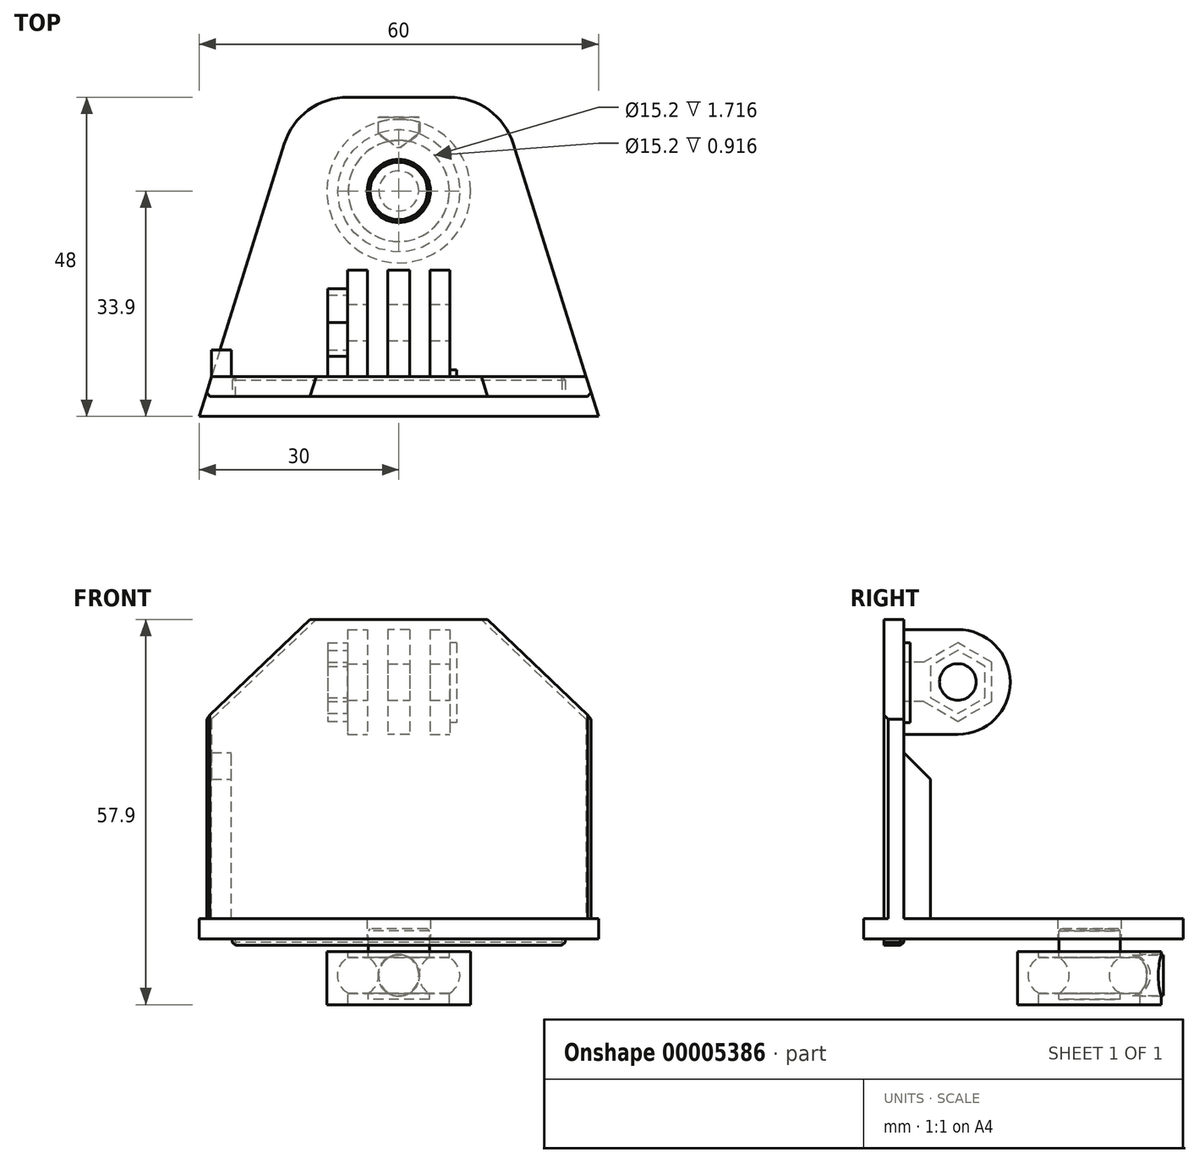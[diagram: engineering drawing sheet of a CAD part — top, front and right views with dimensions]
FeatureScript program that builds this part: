
annotation { "Feature Type Name" : "Feature", "Feature Type Description" : "" }
export const myFeature = defineFeature(function(context is Context, id is Id, definition is map)
    precondition{}
    {
        {
            var Q0;
            Q0=qCreatedBy(makeId("Top.planeOp"),FACE);
            var sketch = newSketch(context, id + "F0", { "sketchPlane" : qUnion([Q0])});
            skArc(sketch, "E0", {"start": v(3, 0) * mm, "mid": v(0, 3) * mm, "end": v(-3, 0) * mm});
            skLineSegment(sketch, "E1", {"start": v(3, 0) * mm, "end": v(-3, 0) * mm});
            skLineSegment(sketch, "E2", {"start": v(0, 0) * mm, "end": v(0, -6.1) * mm, "construction": true});
            skSolve(sketch);
        }
        {
            var Q0;
            Q0=qCreatedBy(makeId("Right.planeOp"),FACE);
            var sketch = newSketch(context, id + "F1", { "sketchPlane" : qUnion([Q0])});
            skCircle(sketch, "E3", {"center": v(0, 0) * mm, "radius": 3.08 * mm});
            skLineSegment(sketch, "E4", {"start": v(0, 0) * mm, "end": v(-12.4, 0) * mm, "construction": true});
            skLineSegment(sketch, "E5", {"start": v(-12.4, 8.14) * mm, "end": v(-12.4, -5.03) * mm, "construction": true});
            skLineSegment(sketch, "E6", {"start": v(0, 0) * mm, "end": v(0, 3.76) * mm, "construction": true});
            skLineSegment(sketch, "E7", {"start": v(-6.1, 3.76) * mm, "end": v(-6.1, -2.41) * mm, "construction": true});
            skSolve(sketch);
        }
        {
            var Q0;
            Q0=sQuery(id+"F1.wireOp",EDGE,"E3");
            var Q1;
            Q1=sQuery(id+"F1.wireOp",EDGE,"E7");
            revolve(context, id + "F2", {"bodyType" : ToolBodyType.SURFACE, "surfaceEntities" : qUnion([Q0]), "axis" : qUnion([Q1]), "revolveType" : RevolveType.FULL});
        }
        {
            var Q0;
            Q0=qCreatedBy(makeId("Right.planeOp"),FACE);
            var sketch = newSketch(context, id + "F3", { "sketchPlane" : qUnion([Q0])});
            skCircle(sketch, "E8.0", {"center": v(0, 0) * mm, "radius": 3.08 * mm});
            skLineSegment(sketch, "E9.0", {"start": v(-6.1, 3.76) * mm, "end": v(-6.1, -2.41) * mm});
            skLineSegment(sketch, "E9.1", {"start": v(0, 0) * mm, "end": v(-12.4, 0) * mm});
            skPoint(sketch, "E10.rect.middle", {"position": v(-6.1, 0) * mm});
            skLineSegment(sketch, "E11", {"start": v(-1.5, 7) * mm, "end": v(-1.5, -3.6) * mm});
            skLineSegment(sketch, "E12", {"start": v(-1.5, -3.6) * mm, "end": v(-6.1, -3.6) * mm});
            skLineSegment(sketch, "E13", {"start": v(-6.1, -3.6) * mm, "end": v(-6.1, 7) * mm});
            skLineSegment(sketch, "E14", {"start": v(-6.1, 7) * mm, "end": v(-1.5, 7) * mm});
            skLineSegment(sketch, "E15", {"start": v(4.7, 3.6) * mm, "end": v(4.7, -4.4) * mm});
            skLineSegment(sketch, "E16", {"start": v(4.7, -4.4) * mm, "end": v(1.5, -4.4) * mm});
            skLineSegment(sketch, "E17", {"start": v(4.7, 3.6) * mm, "end": v(1.5, 3.6) * mm});
            skLineSegment(sketch, "E18", {"start": v(1.5, 3.6) * mm, "end": v(1.5, -4.4) * mm});
            skSolve(sketch);
        }
        {
            var Q0;
            {var subQ0=sQuery(id+"F3.wireOp",EDGE,"E14");Q0=makeQuery(id+"F3.imprint","IMPRINT",FACE,{"disambiguationData":[TD([[makeQuery(id+"F3.imprint","IMPRINT",EDGE,{"derivedFrom":subQ0}),-1.0]])]});}
            var Q1;
            {var subQ3=sQuery(id+"F3.wireOp",EDGE,"E12");Q1=makeQuery(id+"F3.imprint","IMPRINT",FACE,{"disambiguationData":[TD([[makeQuery(id+"F3.imprint","IMPRINT",EDGE,{"derivedFrom":subQ3}),-1.0]])]});}
            var Q2;
            Q2=sQuery(id+"F3.wireOp",EDGE,"E9.0");
            revolve(context, id + "F4", {"entities" : qUnion([Q0, Q1]), "axis" : qUnion([Q2]), "revolveType" : RevolveType.FULL});
        }
        {
            var Q0;
            Q0=makeQuery(id+"F3.imprint","IMPRINT",FACE,{"disambiguationData":[TD([[makeQuery(id+"F3.imprint","IMPRINT",EDGE,{"derivedFrom":sQuery(id+"F3.wireOp",EDGE,"E15")}),-1.0]])]});
            var Q1;
            Q1=sQuery(id+"F3.wireOp",EDGE,"E9.0");
            revolve(context, id + "F5", {"entities" : qUnion([Q0]), "axis" : qUnion([Q1]), "revolveType" : RevolveType.FULL});
        }
        {
            var Q0;
            Q0=qCreatedBy(makeId("Front.planeOp"),FACE);
            var sketch = newSketch(context, id + "F6", { "sketchPlane" : qUnion([Q0])});
            skCircle(sketch, "E19", {"center": v(0, 0) * mm, "radius": 3.15 * mm});
            skSolve(sketch);
        }
        {
            var Q0;
            Q0=makeQuery(id+"F6.imprint","IMPRINT",FACE,{"disambiguationData":[TD([[makeQuery(id+"F6.imprint","IMPRINT",EDGE,{"derivedFrom":sQuery(id+"F6.wireOp",EDGE,"E19")}),1.0]])]});
            var Q1;
            Q1=makeQuery(id+"F5.opRevolve","SWEPT_FACE",FACE,{"disambiguationData":[OSD([sQuery(id+"F3.wireOp",EDGE,"E15")])]});
            extrude(context, id + "F7", {"entities" : qUnion([Q0]), "operationType" : NewBodyOperationType.REMOVE, "endBound" : BoundingType.UP_TO_SURFACE, "oppositeDirection" : true, "endBoundEntityFace" : qUnion([Q1]), "depth" : 25 * mm});
        }
        {
            var Q0;
            Q0=qCreatedBy(makeId("Front.planeOp"),FACE);
            var sketch = newSketch(context, id + "F8", { "sketchPlane" : qUnion([Q0])});
            skLineSegment(sketch, "E20.rect.bottom", {"start": v(13.05, 1.97) * mm, "end": v(8.99, 1.97) * mm});
            skLineSegment(sketch, "E20.rect.top", {"start": v(13.05, 8.89) * mm, "end": v(8.99, 8.89) * mm});
            skLineSegment(sketch, "E20.rect.left", {"start": v(13.05, 1.97) * mm, "end": v(13.05, 8.89) * mm});
            skLineSegment(sketch, "E20.rect.right", {"start": v(8.99, 1.97) * mm, "end": v(8.99, 8.89) * mm});
            skPoint(sketch, "E20.rect.middle", {"position": v(11.02, 5.43) * mm});
            skSolve(sketch);
        }
        {
            var Q0;
            Q0=makeQuery(id+"F8.imprint","IMPRINT",FACE,{"disambiguationData":[TD([[makeQuery(id+"F8.imprint","IMPRINT",EDGE,{"derivedFrom":sQuery(id+"F8.wireOp",EDGE,"E20.rect.bottom")}),-1.0]])]});
            cPlane(context, id + "F9", {"entities" : qUnion([Q0]), "cplaneType" : CPlaneType.OFFSET, "offset" : 5 * mm, "oppositeDirection" : true, "width" : 150 * mm, "height" : 150 * mm});
        }
        {
            var Q0;
            Q0=qCreatedBy(id+"F9.planeOp",FACE);
            var sketch = newSketch(context, id + "F10", { "sketchPlane" : qUnion([Q0])});
            skCircle(sketch, "E21", {"center": v(0, 0) * mm, "radius": 3.05 * mm});
            skSolve(sketch);
        }
        {
            var Q0;
            Q0=makeQuery(id+"F10.imprint","IMPRINT",FACE,{"disambiguationData":[TD([[makeQuery(id+"F10.imprint","IMPRINT",EDGE,{"derivedFrom":sQuery(id+"F10.wireOp",EDGE,"E21")}),1.0]])]});
            var Q1;
            Q1=makeQuery(id+"F5.opRevolve","SWEPT_FACE",FACE,{"disambiguationData":[OSD([sQuery(id+"F3.wireOp",EDGE,"E8.0")])]});
            extrude(context, id + "F11", {"entities" : qUnion([Q0]), "endBound" : BoundingType.UP_TO_SURFACE, "endBoundEntityFace" : qUnion([Q1]), "depth" : 25 * mm});
        }
        {
            var Q0;
            Q0=makeQuery(id+"F4.opRevolve","SWEPT_EDGE",EDGE,{"disambiguationData":[OSD([sQuery(id+"F3.wireOp",EDGE,"E11"),sQuery(id+"F3.wireOp",EDGE,"E14")])]});
            chamfer(context, id + "F12", {"entities" : qUnion([Q0]), "width" : 0.3 * mm, "tangentPropagation" : true});
        }
        {
            var Q0;
            Q0=makeQuery(id+"F4.opRevolve","SWEPT_FACE",FACE,{"disambiguationData":[OSD([sQuery(id+"F3.wireOp",EDGE,"E14")])]});
            var sketch = newSketch(context, id + "F13", { "sketchPlane" : qUnion([Q0])});
            skLineSegment(sketch, "E22.bottom", {"start": v(-25, -34) * mm, "end": v(25, -34) * mm});
            skLineSegment(sketch, "E22.top", {"start": v(-25, -37) * mm, "end": v(25, -37) * mm});
            skLineSegment(sketch, "E22.left", {"start": v(-25, -34) * mm, "end": v(-25, -37) * mm});
            skLineSegment(sketch, "E22.right", {"start": v(25, -34) * mm, "end": v(25, -37) * mm});
            skLineSegment(sketch, "E23", {"start": v(-30, -40) * mm, "end": v(30, -40) * mm});
            skLineSegment(sketch, "E24", {"start": v(-15, 8) * mm, "end": v(15, 8) * mm});
            skLineSegment(sketch, "E25", {"start": v(-15, 8) * mm, "end": v(-30, -40) * mm});
            skLineSegment(sketch, "E26", {"start": v(15, 8) * mm, "end": v(30, -40) * mm});
            skCircle(sketch, "E27.0", {"center": v(0, -6.1) * mm, "radius": 4.75 * mm});
            skSolve(sketch);
        }
        {
            var Q0;
            Q0=makeQuery(id+"F13.imprint","IMPRINT",FACE,{"disambiguationData":[TD([[makeQuery(id+"F13.imprint","IMPRINT",EDGE,{"derivedFrom":sQuery(id+"F13.wireOp",EDGE,"E22.bottom")}),1.0]])]});
            extrude(context, id + "F14", {"entities" : qUnion([Q0]), "endBound" : BoundingType.SYMMETRIC, "depth" : 3 * mm});
        }
        {
            var Q0;
            Q0=makeQuery(id+"F14.opExtrude","SWEPT_EDGE",EDGE,{"disambiguationData":[OSD([sQuery(id+"F13.wireOp",EDGE,"E24"),sQuery(id+"F13.wireOp",EDGE,"E25")])]});
            var Q1;
            Q1=makeQuery(id+"F14.opExtrude","SWEPT_EDGE",EDGE,{"disambiguationData":[OSD([sQuery(id+"F13.wireOp",EDGE,"E24"),sQuery(id+"F13.wireOp",EDGE,"E26")])]});
            fillet(context, id + "F15", {"entities" : qUnion([Q0, Q1]), "radius" : 10 * mm, "tangentPropagation" : true, "allowEdgeOverflow" : false});
        }
        {
            var Q0;
            Q0=makeQuery(id+"F14.opExtrude","CAP_FACE",FACE,{"disambiguationData":[OSD([sQuery(id+"F13.wireOp",EDGE,"E22.bottom"),sQuery(id+"F13.wireOp",EDGE,"E22.top"),sQuery(id+"F13.wireOp",EDGE,"E22.left"),sQuery(id+"F13.wireOp",EDGE,"E22.right"),sQuery(id+"F13.wireOp",EDGE,"E23"),sQuery(id+"F13.wireOp",EDGE,"E24"),sQuery(id+"F13.wireOp",EDGE,"E25"),sQuery(id+"F13.wireOp",EDGE,"E26"),sQuery(id+"F13.wireOp",EDGE,"E27.0")])],"isStart":false});
            var sketch = newSketch(context, id + "F16", { "sketchPlane" : qUnion([Q0])});
            skLineSegment(sketch, "E28.0", {"start": v(-25, -37) * mm, "end": v(25, -37) * mm});
            skLineSegment(sketch, "E28.1", {"start": v(-25, -34) * mm, "end": v(-25, -37) * mm});
            skLineSegment(sketch, "E28.2", {"start": v(-25, -34) * mm, "end": v(25, -34) * mm});
            skLineSegment(sketch, "E28.3", {"start": v(25, -34) * mm, "end": v(25, -37) * mm});
            skLineSegment(sketch, "E29", {"start": v(-25, -34) * mm, "end": v(-28.12, -34) * mm});
            skLineSegment(sketch, "E30", {"start": v(-28.12, -34) * mm, "end": v(-29.06, -37) * mm});
            skLineSegment(sketch, "E31", {"start": v(-29.06, -37) * mm, "end": v(-25, -37) * mm});
            skLineSegment(sketch, "E32", {"start": v(25, -34) * mm, "end": v(28.12, -34) * mm});
            skLineSegment(sketch, "E33", {"start": v(28.12, -34) * mm, "end": v(29.06, -37) * mm});
            skLineSegment(sketch, "E34", {"start": v(29.06, -37) * mm, "end": v(25, -37) * mm});
            skSolve(sketch);
        }
        {
            var Q0;
            Q0=makeQuery(id+"F16.imprint","IMPRINT",FACE,{"disambiguationData":[TD([[makeQuery(id+"F16.imprint","IMPRINT",EDGE,{"derivedFrom":sQuery(id+"F16.wireOp",EDGE,"E28.3")}),1.0]])]});
            var Q1;
            Q1=makeQuery(id+"F16.imprint","IMPRINT",FACE,{"disambiguationData":[TD([[makeQuery(id+"F16.imprint","IMPRINT",EDGE,{"derivedFrom":sQuery(id+"F16.wireOp",EDGE,"E28.1")}),-1.0]])]});
            var Q2;
            Q2=makeQuery(id+"F16.imprint","IMPRINT",FACE,{"disambiguationData":[TD([[makeQuery(id+"F16.imprint","IMPRINT",EDGE,{"derivedFrom":sQuery(id+"F16.wireOp",EDGE,"E28.0")}),1.0]])]});
            extrude(context, id + "F17", {"entities" : qUnion([Q0, Q1, Q2]), "depth" : 45 * mm});
        }
        {
            var Q0;
            Q0=makeQuery(id+"F16.imprint","IMPRINT",FACE,{"disambiguationData":[TD([[makeQuery(id+"F16.imprint","IMPRINT",EDGE,{"derivedFrom":sQuery(id+"F16.wireOp",EDGE,"E28.0")}),1.0]])]});
            var Q1;
            Q1=makeQuery(id+"F14.opExtrude","CAP_FACE",FACE,{"disambiguationData":[OSD([sQuery(id+"F13.wireOp",EDGE,"E22.bottom"),sQuery(id+"F13.wireOp",EDGE,"E22.top"),sQuery(id+"F13.wireOp",EDGE,"E22.left"),sQuery(id+"F13.wireOp",EDGE,"E22.right"),sQuery(id+"F13.wireOp",EDGE,"E23"),sQuery(id+"F13.wireOp",EDGE,"E24"),sQuery(id+"F13.wireOp",EDGE,"E25"),sQuery(id+"F13.wireOp",EDGE,"E26"),sQuery(id+"F13.wireOp",EDGE,"E27.0")])],"isStart":true});
            extrude(context, id + "F18", {"entities" : qUnion([Q0]), "operationType" : NewBodyOperationType.ADD, "oppositeDirection" : true, "endBoundEntity" : qUnion([Q1]), "depth" : 4 * mm});
        }
        {
            var Q0;
            Q0=makeQuery(id+"F18.opExtrude","SWEPT_EDGE",EDGE,{"disambiguationData":[OSD([sQuery(id+"F16.wireOp",EDGE,"E28.2"),sQuery(id+"F16.wireOp",EDGE,"E28.3"),sQuery(id+"F16.wireOp",EDGE,"E32")])]});
            var Q1;
            Q1=makeQuery(id+"F18.opExtrude","SWEPT_EDGE",EDGE,{"disambiguationData":[OSD([sQuery(id+"F16.wireOp",EDGE,"E28.1"),sQuery(id+"F16.wireOp",EDGE,"E28.2"),sQuery(id+"F16.wireOp",EDGE,"E29")])]});
            var Q2;
            Q2=makeQuery(id+"F18.opExtrude","CAP_EDGE",EDGE,{"disambiguationData":[OSD([sQuery(id+"F16.wireOp",EDGE,"E28.2")])],"isStart":false});
            var Q3;
            Q3=makeQuery(id+"F18.opExtrude","CAP_EDGE",EDGE,{"disambiguationData":[OSD([sQuery(id+"F16.wireOp",EDGE,"E28.3")])],"isStart":false});
            var Q4;
            Q4=makeQuery(id+"F18.opExtrude","CAP_EDGE",EDGE,{"disambiguationData":[OSD([sQuery(id+"F16.wireOp",EDGE,"E28.1")])],"isStart":false});
            chamfer(context, id + "F19", {"entities" : qUnion([Q0, Q1, Q2, Q3, Q4]), "width" : 0.5 * mm, "tangentPropagation" : true});
        }
        {
            var Q0;
            Q0=makeQuery(id+"F17.opExtrude","SWEPT_EDGE",EDGE,{"disambiguationData":[OSD([sQuery(id+"F13.wireOp",EDGE,"E26"),sQuery(id+"F16.wireOp",EDGE,"E33"),sQuery(id+"F16.wireOp",EDGE,"E34")])]});
            var Q1;
            Q1=makeQuery(id+"F17.opExtrude","SWEPT_EDGE",EDGE,{"disambiguationData":[OSD([sQuery(id+"F13.wireOp",EDGE,"E25"),sQuery(id+"F16.wireOp",EDGE,"E30"),sQuery(id+"F16.wireOp",EDGE,"E31")])]});
            chamfer(context, id + "F20", {"entities" : qUnion([Q0, Q1]), "width" : 0.5 * mm, "tangentPropagation" : true});
        }
        {
            var Q0;
            {var subQ0=sQuery(id+"F16.wireOp",EDGE,"E28.2");Q0=makeQuery(id+"F18.boolean.opBoolean","MERGE",FACE,{"derivedFrom":[makeQuery(id+"F17.opExtrude","SWEPT_FACE",FACE,{"disambiguationData":[OSD([subQ0,sQuery(id+"F16.wireOp",EDGE,"E29"),sQuery(id+"F16.wireOp",EDGE,"E32")])]}),makeQuery(id+"F18.opExtrude","SWEPT_FACE",FACE,{"disambiguationData":[OSD([subQ0])]})]});}
            var sketch = newSketch(context, id + "F21", { "sketchPlane" : qUnion([Q0])});
            skLineSegment(sketch, "E35.rect.bottom", {"start": v(-1.65, 51.98) * mm, "end": v(1.65, 51.98) * mm});
            skLineSegment(sketch, "E35.rect.top", {"start": v(-1.65, 36.23) * mm, "end": v(1.65, 36.23) * mm});
            skLineSegment(sketch, "E35.rect.left", {"start": v(-1.65, 51.98) * mm, "end": v(-1.65, 36.23) * mm});
            skLineSegment(sketch, "E35.rect.right", {"start": v(1.65, 51.98) * mm, "end": v(1.65, 36.23) * mm});
            skPoint(sketch, "E35.rect.middle", {"position": v(0, 44.1) * mm});
            skLineSegment(sketch, "E36.bottom", {"start": v(-4.7, 51.98) * mm, "end": v(-7.7, 51.98) * mm});
            skLineSegment(sketch, "E36.top", {"start": v(-4.7, 36.23) * mm, "end": v(-7.7, 36.23) * mm});
            skLineSegment(sketch, "E36.left", {"start": v(-4.7, 51.98) * mm, "end": v(-4.7, 36.23) * mm});
            skLineSegment(sketch, "E36.right", {"start": v(-7.7, 51.98) * mm, "end": v(-7.7, 36.23) * mm});
            skLineSegment(sketch, "E37.bottom", {"start": v(7.7, 51.98) * mm, "end": v(4.7, 51.98) * mm});
            skLineSegment(sketch, "E37.top", {"start": v(7.7, 36.23) * mm, "end": v(4.7, 36.23) * mm});
            skLineSegment(sketch, "E37.left", {"start": v(7.7, 51.98) * mm, "end": v(7.7, 36.23) * mm});
            skLineSegment(sketch, "E37.right", {"start": v(4.7, 51.98) * mm, "end": v(4.7, 36.23) * mm});
            skSolve(sketch);
        }
        {
            var Q0;
            Q0=makeQuery(id+"F21.imprint","IMPRINT",FACE,{"disambiguationData":[TD([[makeQuery(id+"F21.imprint","IMPRINT",EDGE,{"derivedFrom":sQuery(id+"F21.wireOp",EDGE,"E36.bottom")}),1.0]])]});
            var Q1;
            Q1=makeQuery(id+"F21.imprint","IMPRINT",FACE,{"disambiguationData":[TD([[makeQuery(id+"F21.imprint","IMPRINT",EDGE,{"derivedFrom":sQuery(id+"F21.wireOp",EDGE,"E35.rect.bottom")}),-1.0]])]});
            var Q2;
            Q2=makeQuery(id+"F21.imprint","IMPRINT",FACE,{"disambiguationData":[TD([[makeQuery(id+"F21.imprint","IMPRINT",EDGE,{"derivedFrom":sQuery(id+"F21.wireOp",EDGE,"E37.bottom")}),1.0]])]});
            extrude(context, id + "F22", {"entities" : qUnion([Q0, Q1, Q2]), "operationType" : NewBodyOperationType.ADD, "depth" : 16 * mm});
        }
        {
            var Q0;
            {var subQ0=sQuery(id+"F16.wireOp",EDGE,"E28.2");Q0=makeQuery(id+"F18.boolean.opBoolean","MERGE",FACE,{"derivedFrom":[makeQuery(id+"F17.opExtrude","SWEPT_FACE",FACE,{"disambiguationData":[OSD([subQ0,sQuery(id+"F16.wireOp",EDGE,"E29"),sQuery(id+"F16.wireOp",EDGE,"E32")])]}),makeQuery(id+"F18.opExtrude","SWEPT_FACE",FACE,{"disambiguationData":[OSD([subQ0])]})]});}
            var sketch = newSketch(context, id + "F23", { "sketchPlane" : qUnion([Q0])});
            skLineSegment(sketch, "E38.bottom", {"start": v(-28.12, 8.5) * mm, "end": v(-25.12, 8.5) * mm});
            skLineSegment(sketch, "E38.top", {"start": v(-28.13, 33.5) * mm, "end": v(-25.12, 33.5) * mm});
            skLineSegment(sketch, "E38.left", {"start": v(-28.12, 8.5) * mm, "end": v(-28.13, 33.5) * mm});
            skLineSegment(sketch, "E38.right", {"start": v(-25.12, 8.5) * mm, "end": v(-25.12, 33.5) * mm});
            skLineSegment(sketch, "E39.bottom", {"start": v(28.12, 8.5) * mm, "end": v(25.12, 8.5) * mm});
            skLineSegment(sketch, "E39.top", {"start": v(28.12, 33.5) * mm, "end": v(25.12, 33.5) * mm});
            skLineSegment(sketch, "E39.left", {"start": v(28.12, 8.5) * mm, "end": v(28.12, 33.5) * mm});
            skLineSegment(sketch, "E39.right", {"start": v(25.12, 8.5) * mm, "end": v(25.12, 33.5) * mm});
            skSolve(sketch);
        }
        {
            var Q0;
            {Q0=qUnion([makeQuery(id+"F23.imprint","IMPRINT",FACE,{"disambiguationData":[TD([[makeQuery(id+"F23.imprint","IMPRINT",EDGE,{"derivedFrom":sQuery(id+"F23.wireOp",EDGE,"E38.bottom")}),-1.0]])]}),makeQuery(id+"F23.imprint","IMPRINT",FACE,{"disambiguationData":[TD([[makeQuery(id+"F23.imprint","IMPRINT",EDGE,{"derivedFrom":sQuery(id+"F23.wireOp",EDGE,"E39.bottom")}),-1.0]])]})]);}
            extrude(context, id + "F24", {"entities" : qUnion([Q0]), "operationType" : NewBodyOperationType.ADD, "depth" : 4 * mm});
        }
        {
            var Q0;
            Q0=makeQuery(id+"F24.opExtrude","CAP_EDGE",EDGE,{"disambiguationData":[OSD([sQuery(id+"F23.wireOp",EDGE,"E38.top")])],"isStart":false});
            var Q1;
            Q1=makeQuery(id+"F24.opExtrude","CAP_EDGE",EDGE,{"disambiguationData":[OSD([sQuery(id+"F23.wireOp",EDGE,"E39.top")])],"isStart":false});
            chamfer(context, id + "F25", {"entities" : qUnion([Q0, Q1]), "width" : 4 * mm, "tangentPropagation" : true});
        }
        {
            var Q0;
            Q0=makeQuery(id+"F22.opExtrude","SWEPT_FACE",FACE,{"disambiguationData":[OSD([sQuery(id+"F21.wireOp",EDGE,"E36.right")])]});
            var sketch = newSketch(context, id + "F26", { "sketchPlane" : qUnion([Q0])});
            skCircle(sketch, "E40", {"center": v(-25.88, 44.1) * mm, "radius": 2.75 * mm});
            skSolve(sketch);
        }
        {
            var Q0;
            Q0=makeQuery(id+"F26.imprint","IMPRINT",FACE,{"disambiguationData":[TD([[makeQuery(id+"F26.imprint","IMPRINT",EDGE,{"derivedFrom":sQuery(id+"F26.wireOp",EDGE,"E40")}),1.0]])]});
            extrude(context, id + "F27", {"entities" : qUnion([Q0]), "operationType" : NewBodyOperationType.REMOVE, "oppositeDirection" : true, "depth" : 25 * mm});
        }
        {
            var Q0;
            Q0=makeQuery(id+"F22.opExtrude","CAP_EDGE",EDGE,{"disambiguationData":[OSD([sQuery(id+"F21.wireOp",EDGE,"E36.bottom")])],"isStart":false});
            var Q1;
            Q1=makeQuery(id+"F22.opExtrude","CAP_EDGE",EDGE,{"disambiguationData":[OSD([sQuery(id+"F21.wireOp",EDGE,"E35.rect.bottom")])],"isStart":false});
            var Q2;
            Q2=makeQuery(id+"F22.opExtrude","CAP_EDGE",EDGE,{"disambiguationData":[OSD([sQuery(id+"F21.wireOp",EDGE,"E37.bottom")])],"isStart":false});
            var Q3;
            Q3=makeQuery(id+"F22.opExtrude","CAP_EDGE",EDGE,{"disambiguationData":[OSD([sQuery(id+"F21.wireOp",EDGE,"E37.top")])],"isStart":false});
            var Q4;
            Q4=makeQuery(id+"F22.opExtrude","CAP_EDGE",EDGE,{"disambiguationData":[OSD([sQuery(id+"F21.wireOp",EDGE,"E35.rect.top")])],"isStart":false});
            var Q5;
            Q5=makeQuery(id+"F22.opExtrude","CAP_EDGE",EDGE,{"disambiguationData":[OSD([sQuery(id+"F21.wireOp",EDGE,"E36.top")])],"isStart":false});
            fillet(context, id + "F28", {"entities" : qUnion([Q0, Q1, Q2, Q3, Q4, Q5]), "radius" : 7.88 * mm, "tangentPropagation" : true, "allowEdgeOverflow" : false});
        }
        {
            var Q0;
            Q0=makeQuery(id+"F17.opExtrude","CAP_EDGE",EDGE,{"disambiguationData":[OSD([sQuery(id+"F16.wireOp",EDGE,"E30")])],"isStart":false});
            var Q1;
            Q1=makeQuery(id+"F17.opExtrude","CAP_EDGE",EDGE,{"disambiguationData":[OSD([sQuery(id+"F16.wireOp",EDGE,"E33")])],"isStart":false});
            chamfer(context, id + "F29", {"entities" : qUnion([Q0, Q1]), "width" : 15 * mm, "tangentPropagation" : true});
        }
        {
            var Q0;
            Q0=makeQuery(id+"F22.opExtrude","SWEPT_FACE",FACE,{"disambiguationData":[OSD([sQuery(id+"F21.wireOp",EDGE,"E37.left")])]});
            var sketch = newSketch(context, id + "F30", { "sketchPlane" : qUnion([Q0])});
            skCircle(sketch, "E41.0", {"center": v(25.88, 44.1) * mm, "radius": 2.75 * mm});
            skCircle(sketch, "E42.cCircle", {"center": v(25.88, 44.1) * mm, "radius": 4.1 * mm, "construction": true});
            skLineSegment(sketch, "E42.0", {"start": v(29.98, 46.47) * mm, "end": v(29.98, 41.73) * mm});
            skLineSegment(sketch, "E42.1", {"start": v(29.97, 41.73) * mm, "end": v(25.88, 39.37) * mm});
            skLineSegment(sketch, "E42.2", {"start": v(25.88, 39.37) * mm, "end": v(21.78, 41.73) * mm});
            skLineSegment(sketch, "E42.3", {"start": v(21.78, 41.73) * mm, "end": v(21.78, 46.47) * mm});
            skLineSegment(sketch, "E42.4", {"start": v(21.78, 46.47) * mm, "end": v(25.88, 48.83) * mm});
            skLineSegment(sketch, "E42.5", {"start": v(25.88, 48.83) * mm, "end": v(29.98, 46.47) * mm});
            skPoint(sketch, "E42.0.midPoint", {"position": v(29.98, 44.1) * mm});
            skLineSegment(sketch, "E43.0", {"start": v(20.78, 47.04) * mm, "end": v(25.88, 49.99) * mm});
            skLineSegment(sketch, "E43.1", {"start": v(20.78, 41.16) * mm, "end": v(20.78, 47.04) * mm});
            skLineSegment(sketch, "E43.2", {"start": v(25.88, 38.21) * mm, "end": v(20.78, 41.16) * mm});
            skLineSegment(sketch, "E43.3", {"start": v(30.98, 41.16) * mm, "end": v(25.88, 38.21) * mm});
            skLineSegment(sketch, "E43.4", {"start": v(30.97, 47.04) * mm, "end": v(30.97, 41.16) * mm});
            skLineSegment(sketch, "E43.5", {"start": v(25.88, 49.99) * mm, "end": v(30.97, 47.04) * mm});
            skLineSegment(sketch, "E44.bottom", {"start": v(30.98, 41.16) * mm, "end": v(34, 41.16) * mm});
            skLineSegment(sketch, "E44.top", {"start": v(30.98, 47.04) * mm, "end": v(34, 47.04) * mm});
            skLineSegment(sketch, "E44.left", {"start": v(30.98, 41.16) * mm, "end": v(30.98, 47.04) * mm});
            skLineSegment(sketch, "E44.right", {"start": v(34, 41.16) * mm, "end": v(34, 47.04) * mm});
            skSolve(sketch);
        }
        {
            var Q0;
            Q0=makeQuery(id+"F30.imprint","IMPRINT",FACE,{"disambiguationData":[TD([[makeQuery(id+"F30.imprint","IMPRINT",EDGE,{"derivedFrom":sQuery(id+"F30.wireOp",EDGE,"E42.0")}),1.0]])]});
            var Q1;
            Q1=makeQuery(id+"F30.imprint","IMPRINT",FACE,{"disambiguationData":[TD([[makeQuery(id+"F30.imprint","IMPRINT",EDGE,{"derivedFrom":sQuery(id+"F30.wireOp",EDGE,"E44.bottom")}),1.0]])]});
            extrude(context, id + "F31", {"entities" : qUnion([Q0, Q1]), "operationType" : NewBodyOperationType.ADD, "depth" : 3 * mm});
        }
        {
            var Q0;
            Q0=makeQuery(id+"F22.opExtrude","SWEPT_FACE",FACE,{"disambiguationData":[OSD([sQuery(id+"F21.wireOp",EDGE,"E36.right")])]});
            var sketch = newSketch(context, id + "F32", { "sketchPlane" : qUnion([Q0])});
            skLineSegment(sketch, "E45.bottom", {"start": v(-33, 49.98) * mm, "end": v(-34, 49.98) * mm});
            skLineSegment(sketch, "E45.top", {"start": v(-33, 37.97) * mm, "end": v(-34, 37.97) * mm});
            skLineSegment(sketch, "E45.left", {"start": v(-33, 49.98) * mm, "end": v(-33, 37.97) * mm});
            skLineSegment(sketch, "E45.right", {"start": v(-34, 49.97) * mm, "end": v(-34, 37.97) * mm});
            skSolve(sketch);
        }
        {
            var Q0;
            Q0=makeQuery(id+"F32.imprint","IMPRINT",FACE,{"disambiguationData":[TD([[makeQuery(id+"F32.imprint","IMPRINT",EDGE,{"derivedFrom":sQuery(id+"F32.wireOp",EDGE,"E45.bottom")}),1.0]])]});
            extrude(context, id + "F33", {"entities" : qUnion([Q0]), "operationType" : NewBodyOperationType.ADD, "depth" : 1 * mm});
        }
    });
